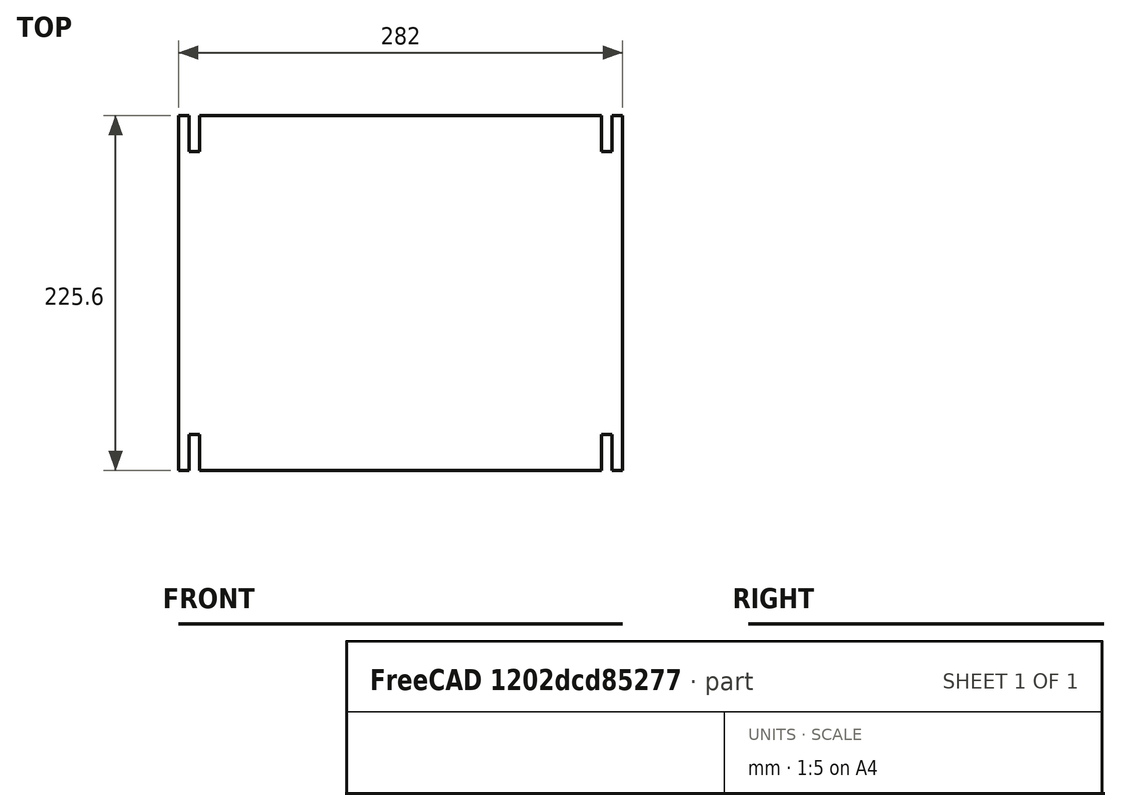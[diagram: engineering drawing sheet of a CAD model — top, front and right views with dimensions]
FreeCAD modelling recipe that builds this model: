
FCSTD DOCUMENT  (FreeCAD 0.17R13522 (Git))
Label: chamber_parts
License: All rights reserved
LicenseURL: http://en.wikipedia.org/wiki/All_rights_reserved
objects: Part::Part2DObjectPython×15, Part::FeaturePython×9, App::DocumentObjectGroup×6, Sketcher::SketchObject×3, Part::Compound×2, Part::Feature×2, Spreadsheet::Sheet×1, Part::MultiFuse×1, Drawing::FeatureViewPython×1, Drawing::FeaturePage×1, App::Part×1, Part::Cut×1
note: 33 computed .brp shape members not serialized (recipe doc carries the construction recipe); baked Part::Feature solids carry a one-line shape summary decoded from their .brp

FEATURE [Spreadsheet::Sheet] Spreadsheet  label="params"
  cells = A1=Name / alias; B1=Value; C1=Note; A2=extrusion_width; B2(extrusion_width)==20mm; A3=extrusion_x_spacer_length; B3(extrusion_spacer_length)==242mm; A4=mfc_mounting_hole_dx; B4(mfc_mounting_hole_dx)==52.710000000000001mm; C4=From MFC technical drawing (56.52 - 3.81mm); A5=mfc_mounting_hole_dy; B5(mfc_mounting_hole_dy)==20.32mm; A6=mfc_z_extent; B6(mfc_z_extent)==103.3mm; A7=mfc_y_extent; B7(mfc_y_extent)==26.68mm; A8=humidifier_bottle_diameter; B8(humidifier_bottle_diameter)==70mm; A9=humidifier_bottle_and_tube_height; B9(humidifier_bottle_and_tube_height)==230mm; A10=shelf_y_extent; B10(shelf_y_extent)==80mm; C10=Seems to need to be at least ~80mm, if I want at least 3 mounting holes, spaced with current rules.; A11=mfc_mounting_screw_clearance_diam; B11(mfc_mounting_screw_clearance_diam)==0.16950000000000001in; C11="Close fit" for 8-32; A12=mfc_x_extent; B12(mfc_x_extent)==94.950000000000003mm; A13=x_between_mfc_for_tubing; B13(x_between_mfc_for_tubing)==70mm; C13=Should allow space for 1 inlet fitting + 1 outlet fitting + the tubing to bend and get out of the way.; A14=y_mfc_to_edge_clearance; B14(y_mfc_to_edge_clearance)==14mm; C14=To allow one extrusion mounting hole to fit on other side, plus some.; A15=y_mfc_mounting_hole_center_to_edge; B15(y_mfc_mounting_hole_center_to_edge)==3.1800000000000002mm; C15=From MFC technical drawing (?); A16=x_mfc_row_offset; B16(x_mfc_row_offset)==53mm; A17=extrusion_mounting_hole_diam; B17(extrusion_mounting_hole_diam)==0.25700000000000001in; C17=max(1/4-20 clearance, M5 clearance); A18=extrusion_mounting_hole_to_edge_clearance; B18(extrusion_mounting_hole_to_edge_clearance)==4.5mm; A19=n_extrusion_mounting_holes_per_side; B19(n_extrusion_mounting_holes_per_side)=2; A20=fillet_radius; B20(fillet_radius)==4mm; A21=mfc_array_x_origin; B21(mfc_array_x_origin)==-152mm; A22=mounting_hole_spacing; B22(mounting_hole_spacing)==4.5mm; C22=Minimum amount of material along the line between two mounting holes.; A23=humidifier_bottle_spacing; B23(humidifier_bottle_spacing)==0mm; C23=Similar to above.; A24=n_humidifier_bottles; B24(n_humidifier_bottles)=4; A25=inside_plate_edge_clearance; B25(inside_plate_edge_clearance)==1.5mm; A26=extrusion_y_spacer_length; B26(extrusion_y_spacer_length)==228.59999999999999mm; A27=mounting_slot_length; B27(mounting_slot_length)==23mm; A28=shelf_x_beyond_extrusion; B28(shelf_x_beyond_extrusion)==20mm; C28=On either side (this is added to shelf x extent twice).; A29=box_height; B29(box_height)==381mm; C29=15 inches; A30=olfactometer_tube_passthru_diam; B30(olfactometer_tube_passthru_diam)==12mm; A31=chamber_support_rail_top_height; B31(chamber_support_rail_top_height)==146mm; C31=Up the length of the box_height length vertical rails.; A32=olfactometer_tube_passthru_height; B32(olfactometer_tube_passthru_height)==40mm; C32=Top of chamber support rail to center of hole.; A33=vacuum_tube_passthru_height; B33(vacuum_tube_passthru_height)==200mm; C33=Same as above.; A34=vacuum_tube_passthru_diam; B34(vacuum_tube_passthru_diam)==12mm; A35=n_mounting_holes_half_side; B35(n_mounting_holes_half_side)=5; C35=The number of mounting holes on each side of each side panel (i.e. the number in one row,  mounting to one rail).; A36=side_mounting_hole_edge_clearance; B36(side_mounting_hole_edge_clearance)==15mm
FEATURE [Part::Part2DObjectPython] Circle  label="mfc_back_mounting_hole"  # Draft 2D object (typed FeaturePython)
  FirstAngle = 0
  LastAngle = 0
  MakeFace = false
  Placement = pos=(0,20.32,0) rot=(0,0,1;0rad)
  Radius = 2.15265
  expr: Placement.Base.y = params.mfc_mounting_hole_dy
  expr: Placement.Base.x = 0
  expr: Radius = params.mfc_mounting_screw_clearance_diam / 2
FEATURE [Part::Part2DObjectPython] Circle001  label="mfc_front_mounting_hole"  # Draft 2D object (typed FeaturePython)
  FirstAngle = 0
  LastAngle = 0
  MakeFace = false
  Placement = pos=(52.71,0,0) rot=(0,0,1;0rad)
  Radius = 2.15265
  expr: Placement.Base.y = mfc_back_mounting_hole.Placement.Base.y - params.mfc_mounting_hole_dy
  expr: Placement.Base.x = mfc_back_mounting_hole.Placement.Base.x + params.mfc_mounting_hole_dx
  expr: Radius = params001.mfc_mounting_screw_clearance_diam / 2
FEATURE [Part::MultiFuse] Fusion  label="mfc_mounting_holes"
  Shapes = -> [Circle,Circle001]
  expr: Placement.Base.y = 0
  expr: Placement.Base.x = 0
FEATURE [Part::FeaturePython] Array  label="back_two_mfc_mounting_holes"  # Draft array (typed FeaturePython)
  Angle = 360
  ArrayType = 0
  Axis = (0,0,1)
  Base = -> Fusion
  Center = (0,0,0)
  Fuse = false
  IntervalAxis = (0,0,0)
  IntervalX = (164.95,0,0)
  IntervalY = (0,1,0)
  IntervalZ = (0,0,0)
  NumberPolar = 1
  NumberX = 2
  NumberY = 1
  NumberZ = 1
  Placement = pos=(-152,17.18,0) rot=(0,0,1;0rad)
  expr: Placement.Base.y = params.y_mfc_mounting_hole_center_to_edge + params.y_mfc_to_edge_clearance
  expr: Placement.Base.x = params.mfc_array_x_origin
  expr: Center.x = 0
  expr: IntervalX.x = params.mfc_x_extent + params.x_between_mfc_for_tubing
FEATURE [Part::FeaturePython] Array001  label="front_two_mfc_mounting_holes"  # Draft array (typed FeaturePython)
  Angle = 360
  ArrayType = 0
  Axis = (0,0,1)
  Base = -> Fusion
  Center = (0,0,0)
  Fuse = false
  IntervalAxis = (0,0,0)
  IntervalX = (164.95,0,0)
  IntervalY = (0,1,0)
  IntervalZ = (0,0,0)
  NumberPolar = 1
  NumberX = 2
  NumberY = 1
  NumberZ = 1
  Placement = pos=(-99,43.86,0) rot=(0,0,1;0rad)
  expr: Placement.Base.x = back_two_mfc_mounting_holes.Placement.Base.x + params.x_mfc_row_offset
  expr: Placement.Base.y = back_two_mfc_mounting_holes.Placement.Base.y + params.mfc_y_extent
  expr: Center.x = 0
  expr: IntervalX.x = params.mfc_x_extent + params.x_between_mfc_for_tubing
FEATURE [Part::Part2DObjectPython] Circle002  label="extrusion_mounting_hole"  # Draft 2D object (typed FeaturePython)
  FirstAngle = 0
  LastAngle = 0
  MakeFace = false
  Radius = 3.2639
  expr: Radius = params.extrusion_mounting_hole_diam / 2
FEATURE [Part::FeaturePython] Array002  label="extrusion_mounting_holes_left"  # Draft array (typed FeaturePython)
  Angle = 360
  ArrayType = 0
  Axis = (0,0,1)
  Base = -> Circle002
  Center = (0,0,0)
  Fuse = false
  IntervalAxis = (0,0,0)
  IntervalX = (131,0,0)
  IntervalY = (0,64.4722,0)
  IntervalZ = (0,0,0)
  NumberPolar = 1
  NumberX = 2
  NumberY = 2
  NumberZ = 1
  Placement = pos=(-131,7.7639,0) rot=(-0.894427,0,0.447214;0rad)
  expr: Placement.Base.x = -1 * (params.extrusion_spacer_length + params.extrusion_width) / 2
  expr: IntervalX.x = (params.extrusion_spacer_length + params.extrusion_width) / 2
  expr: NumberY = params.n_extrusion_mounting_holes_per_side
  expr: Placement.Base.y = params.extrusion_mounting_hole_diam / 2 + params.extrusion_mounting_hole_to_edge_clearance
  expr: IntervalY.y = (params.shelf_y_extent - params.extrusion_mounting_hole_diam - 2 * params.extrusion_mounting_hole_to_edge_clearance) / (extrusion_mounting_holes_left.NumberY - 1)
FEATURE [Part::FeaturePython] Array003  label="extrusion_mounting_holes_right"  # Draft array (typed FeaturePython)
  Angle = 360
  ArrayType = 0
  Axis = (0,0,1)
  Base = -> Circle002
  Center = (0,0,0)
  Fuse = false
  IntervalAxis = (0,0,0)
  IntervalX = (0,0,0)
  IntervalY = (0,64.4722,0)
  IntervalZ = (0,0,0)
  NumberPolar = 1
  NumberX = 1
  NumberY = 2
  NumberZ = 1
  Placement = pos=(131,7.7639,0) rot=(0,0,1;0rad)
  expr: IntervalX.x = 0
  expr: Placement.Base.y = params.extrusion_mounting_hole_diam / 2 + params.extrusion_mounting_hole_to_edge_clearance
  expr: Placement.Base.x = (params.extrusion_spacer_length + params.extrusion_width) / 2
  expr: IntervalY.y = (params.shelf_y_extent - params.extrusion_mounting_hole_diam - 2 * params.extrusion_mounting_hole_to_edge_clearance) / (extrusion_mounting_holes_right.NumberY - 1)
  expr: NumberY = 2
FEATURE [Sketcher::SketchObject] Sketch  label="mfc_shelf_outline"
  expr: Constraints[27] = params.fillet_radius
  expr: Constraints[26] = params.fillet_radius
  expr: Constraints[25] = params.fillet_radius
  expr: Constraints[12] = -1 / 2 * (params.extrusion_spacer_length + 2 * params.extrusion_width + 2 * params.shelf_x_beyond_extrusion)
  expr: Constraints[24] = params.fillet_radius
  expr: Constraints[10] = params.shelf_y_extent
  expr: Constraints[11] = params.extrusion_spacer_length + 2 * params.extrusion_width + 2 * params.shelf_x_beyond_extrusion
  sketch-geometry (10):
    g0: LineSegment StartX=-157 StartY=1e-12 StartZ=0 EndX=157 EndY=0 EndZ=0
    g1: LineSegment StartX=161 StartY=4 StartZ=0 EndX=161 EndY=76 EndZ=0
    g2: LineSegment StartX=157 StartY=80 StartZ=0 EndX=-157 EndY=80 EndZ=0
    g3: LineSegment StartX=-161 StartY=76 StartZ=0 EndX=-161 EndY=4 EndZ=0
    g4: LineSegment [constr] StartX=-123.644 StartY=80 StartZ=0 EndX=-123.644 EndY=0 EndZ=0
    g5: LineSegment [constr] StartX=-161 StartY=42.4606 StartZ=0 EndX=161 EndY=42.4606 EndZ=0
    g6: ArcOfCircle CenterX=157 CenterY=76 CenterZ=0 NormalX=0 NormalY=0 NormalZ=1 AngleXU=0 Radius=4 StartAngle=0 EndAngle=1.5708
    g7: ArcOfCircle CenterX=157 CenterY=4 CenterZ=0 NormalX=0 NormalY=0 NormalZ=1 AngleXU=0 Radius=4 StartAngle=4.71239 EndAngle=6.28319
    g8: ArcOfCircle CenterX=-157 CenterY=76 CenterZ=0 NormalX=0 NormalY=0 NormalZ=1 AngleXU=0 Radius=4 StartAngle=1.5708 EndAngle=3.14159
    g9: ArcOfCircle CenterX=-157 CenterY=4 CenterZ=0 NormalX=0 NormalY=0 NormalZ=1 AngleXU=0 Radius=4 StartAngle=3.14159 EndAngle=4.71239
  constraints (28):
    c: Vertical(g4)
    c: PointOnObject(g4,g2)
    c: PointOnObject(g4,g0)
    c: Horizontal(g5)
    c: PointOnObject(g5,g1)
    c: PointOnObject(g5,g3)
    c: Perpendicular(g2,g4)
    c: Perpendicular(g0,g4)
    c: Perpendicular(g5,g3)
    c: Perpendicular(g5,g1)
    c: Distance(g4) = 80
    c: Distance(g5) = 322
    c: DistanceX(g5) = -161
    c: DistanceY(g5) = 42.4606
    c: DistanceX(g4) = -123.644
    c: DistanceY(g4) = 0
    c: Tangent(g1,g6) = -1.5708
    c: Tangent(g2,g6) = -1.5708
    c: Tangent(g0,g7) = -1.5708
    c: Tangent(g1,g7) = -1.5708
    c: Tangent(g2,g8) = -1.5708
    c: Tangent(g3,g8) = -1.5708
    c: Tangent(g0,g9) = -1.5708
    c: Tangent(g3,g9) = -1.5708
    c: Radius(g8) = 4
    c: Radius(g6) = 4
    c: Radius(g7) = 4
    c: Radius(g9) = 4
FEATURE [Part::Part2DObjectPython] Circle003  label="hole1"  # Draft 2D object (typed FeaturePython)
  FirstAngle = 0
  LastAngle = 0
  MakeFace = false
  Placement = pos=(-11.0278,72.2361,0) rot=(0,0,1;0rad)
  Radius = 3.2639
  expr: Placement.Base.x = -1 * (params.extrusion_mounting_hole_diam + params.mounting_hole_spacing)
  expr: Placement.Base.y = extrusion_mounting_holes_left.Placement.Base.y + (params.shelf_y_extent - params.extrusion_mounting_hole_diam - 2 * params.extrusion_mounting_hole_to_edge_clearance) / (extrusion_mounting_holes_left.NumberY - 1)
  expr: Radius = params.extrusion_mounting_hole_diam / 2
FEATURE [Part::Part2DObjectPython] Circle004  label="hole2"  # Draft 2D object (typed FeaturePython)
  FirstAngle = 0
  LastAngle = 0
  MakeFace = false
  Placement = pos=(-119.972,7.7639,0) rot=(0,0,1;0rad)
  Radius = 3.2639
  expr: Placement.Base.x = -1 * (params.extrusion_spacer_length + params.extrusion_width) / 2 + params.extrusion_mounting_hole_diam + params.mounting_hole_spacing
  expr: Placement.Base.y = extrusion_mounting_holes_left.Placement.Base.y
  expr: Radius = params.extrusion_mounting_hole_diam / 2
FEATURE [Part::Part2DObjectPython] Circle005  label="hole3"  # Draft 2D object (typed FeaturePython)
  FirstAngle = 0
  LastAngle = 0
  MakeFace = false
  Placement = pos=(119.972,7.7639,0) rot=(0,0,1;0rad)
  Radius = 3.2639
  expr: Placement.Base.x = (params.extrusion_spacer_length + params.extrusion_width) / 2 - (params.extrusion_mounting_hole_diam + params.mounting_hole_spacing)
  expr: Placement.Base.y = extrusion_mounting_holes_left.Placement.Base.y
  expr: Radius = params.extrusion_mounting_hole_diam / 2
FEATURE [Part::Part2DObjectPython] Circle006  label="hole4"  # Draft 2D object (typed FeaturePython)
  FirstAngle = 0
  LastAngle = 0
  MakeFace = false
  Placement = pos=(119.972,72.2361,0) rot=(0,0,1;0rad)
  Radius = 3.2639
  expr: Placement.Base.x = (params.extrusion_spacer_length + params.extrusion_width) / 2 - (params.extrusion_mounting_hole_diam + params.mounting_hole_spacing)
  expr: Placement.Base.y = extrusion_mounting_holes_left.Placement.Base.y + (params.shelf_y_extent - params.extrusion_mounting_hole_diam - 2 * params.extrusion_mounting_hole_to_edge_clearance) / (extrusion_mounting_holes_left.NumberY - 1)
  expr: Radius = params.extrusion_mounting_hole_diam / 2
FEATURE [Sketcher::SketchObject] Sketch001  label="humidifier_shelf_outline"
  expr: Constraints[27] = params.fillet_radius
  expr: Constraints[26] = params.fillet_radius
  expr: Constraints[25] = params.fillet_radius
  expr: Constraints[24] = params.fillet_radius
  expr: Constraints[10] = params.shelf_y_extent
  expr: Constraints[11] = params.extrusion_spacer_length + 2 * params.extrusion_width
  sketch-geometry (10):
    g0: LineSegment StartX=-137 StartY=0 StartZ=0 EndX=137 EndY=0 EndZ=0
    g1: LineSegment StartX=141 StartY=4 StartZ=0 EndX=141 EndY=76 EndZ=0
    g2: LineSegment StartX=137 StartY=80 StartZ=0 EndX=-137 EndY=80 EndZ=0
    g3: LineSegment StartX=-141 StartY=76 StartZ=0 EndX=-141 EndY=4 EndZ=0
    g4: LineSegment [constr] StartX=-123.644 StartY=80 StartZ=0 EndX=-123.644 EndY=0 EndZ=0
    g5: LineSegment [constr] StartX=-141 StartY=42.4606 StartZ=0 EndX=141 EndY=42.4606 EndZ=0
    g6: ArcOfCircle CenterX=137 CenterY=76 CenterZ=0 NormalX=0 NormalY=0 NormalZ=1 AngleXU=0 Radius=4 StartAngle=0 EndAngle=1.5708
    g7: ArcOfCircle CenterX=137 CenterY=4 CenterZ=0 NormalX=0 NormalY=0 NormalZ=1 AngleXU=0 Radius=4 StartAngle=4.71239 EndAngle=6.28319
    g8: ArcOfCircle CenterX=-137 CenterY=76 CenterZ=0 NormalX=0 NormalY=0 NormalZ=1 AngleXU=0 Radius=4 StartAngle=1.5708 EndAngle=3.14159
    g9: ArcOfCircle CenterX=-137 CenterY=4 CenterZ=0 NormalX=0 NormalY=0 NormalZ=1 AngleXU=0 Radius=4 StartAngle=3.14159 EndAngle=4.71239
  constraints (28):
    c: Vertical(g4)
    c: PointOnObject(g4,g2)
    c: PointOnObject(g4,g0)
    c: Horizontal(g5)
    c: PointOnObject(g5,g1)
    c: PointOnObject(g5,g3)
    c: Perpendicular(g2,g4)
    c: Perpendicular(g0,g4)
    c: Perpendicular(g5,g3)
    c: Perpendicular(g5,g1)
    c: Distance(g4) = 80
    c: Distance(g5) = 282
    c: DistanceX(g5) = -141
    c: DistanceY(g5) = 42.4606
    c: DistanceX(g4) = -123.644
    c: DistanceY(g4) = 0
    c: Tangent(g1,g6) = -1.5708
    c: Tangent(g2,g6) = -1.5708
    c: Tangent(g0,g7) = -1.5708
    c: Tangent(g1,g7) = -1.5708
    c: Tangent(g2,g8) = -1.5708
    c: Tangent(g3,g8) = -1.5708
    c: Tangent(g0,g9) = -1.5708
    c: Tangent(g3,g9) = -1.5708
    c: Radius(g8) = 4
    c: Radius(g6) = 4
    c: Radius(g7) = 4
    c: Radius(g9) = 4
FEATURE [Part::Compound] Compound001  label="extrusion_mounting_holes_compound"
  Links = -> [Array003,Array002]
FEATURE [Part::Compound] Compound002  label="extra_mounting_holes_compound"
  Links = -> [Circle003,Circle004,Circle005,Circle006]
FEATURE [App::DocumentObjectGroup] Group002  label="mfc_mounting_plate"
  Group = -> [Sketch,Compound001,Compound002,Array,Array001]
FEATURE [Drawing::FeatureViewPython] ViewGroup002  # drawing view (typed FeaturePython)
  AlwaysOn = false
  Direction = (0,0,0)
  FillStyle = 0
  FontSize = 12
  LineSpacing = 0
  LineStyle = 0
  LineWidth = 0.35
  Rotation = 0
  Source = -> Group002
  ViewResult = <g id="ViewGroup002" transform="rotate(0.0,150.0,150.0) translate(150.0,150.0) scale(1.0,-1.0)"></g>
  Visible = false
  X = 150
  Y = 150
FEATURE [Drawing::FeaturePage] Page  label="printable_view"
  EditableTexts = DRAW_BY | CONTROLLED_BY | DATE | Controlled 2: | CONTROLLED 2 | Controlled 3: | CONTROLLED 3 | SCALE | MOD | COMPANY | ADRESS | COUNTRY | PART NAME | PROJECT NUMBER | A: | A_ | B: | B_ | C: | C_ | D: | D_ | E: | E_ | Quantity | Part ID / number | Fabrication tolerances | Material | 01 | 001 - 001 | ISO2768 - fH | IRON
  Group = -> [ViewGroup002]
  Template = <path>
FEATURE [Sketcher::SketchObject] Sketch002  label="humidifier_bottle_guide_outline"
  expr: Constraints[27] = params.fillet_radius
  expr: Constraints[26] = params.fillet_radius
  expr: Constraints[25] = params.fillet_radius
  expr: Constraints[24] = params.fillet_radius
  expr: Constraints[10] = params.shelf_y_extent
  expr: Constraints[11] = params.extrusion_spacer_length + 2 * params.extrusion_width
  sketch-geometry (10):
    g0: LineSegment StartX=-137 StartY=0 StartZ=0 EndX=137 EndY=0 EndZ=0
    g1: LineSegment StartX=141 StartY=4 StartZ=0 EndX=141 EndY=76 EndZ=0
    g2: LineSegment StartX=137 StartY=80 StartZ=0 EndX=-137 EndY=80 EndZ=0
    g3: LineSegment StartX=-141 StartY=76 StartZ=0 EndX=-141 EndY=4 EndZ=0
    g4: LineSegment [constr] StartX=-123.644 StartY=80 StartZ=0 EndX=-123.644 EndY=0 EndZ=0
    g5: LineSegment [constr] StartX=-141 StartY=42.4606 StartZ=0 EndX=141 EndY=42.4606 EndZ=0
    g6: ArcOfCircle CenterX=137 CenterY=76 CenterZ=0 NormalX=0 NormalY=0 NormalZ=1 AngleXU=0 Radius=4 StartAngle=0 EndAngle=1.5708
    g7: ArcOfCircle CenterX=137 CenterY=4 CenterZ=0 NormalX=0 NormalY=0 NormalZ=1 AngleXU=0 Radius=4 StartAngle=4.71239 EndAngle=6.28319
    g8: ArcOfCircle CenterX=-137 CenterY=76 CenterZ=0 NormalX=0 NormalY=0 NormalZ=1 AngleXU=0 Radius=4 StartAngle=1.5708 EndAngle=3.14159
    g9: ArcOfCircle CenterX=-137 CenterY=4 CenterZ=0 NormalX=0 NormalY=0 NormalZ=1 AngleXU=0 Radius=4 StartAngle=3.14159 EndAngle=4.71239
  constraints (28):
    c: Vertical(g4)
    c: PointOnObject(g4,g2)
    c: PointOnObject(g4,g0)
    c: Horizontal(g5)
    c: PointOnObject(g5,g1)
    c: PointOnObject(g5,g3)
    c: Perpendicular(g2,g4)
    c: Perpendicular(g0,g4)
    c: Perpendicular(g5,g3)
    c: Perpendicular(g5,g1)
    c: Distance(g4) = 80
    c: Distance(g5) = 282
    c: DistanceX(g5) = -141
    c: DistanceY(g5) = 42.4606
    c: DistanceX(g4) = -123.644
    c: DistanceY(g4) = 0
    c: Tangent(g1,g6) = -1.5708
    c: Tangent(g2,g6) = -1.5708
    c: Tangent(g0,g7) = -1.5708
    c: Tangent(g1,g7) = -1.5708
    c: Tangent(g2,g8) = -1.5708
    c: Tangent(g3,g8) = -1.5708
    c: Tangent(g0,g9) = -1.5708
    c: Tangent(g3,g9) = -1.5708
    c: Radius(g8) = 4
    c: Radius(g6) = 4
    c: Radius(g7) = 4
    c: Radius(g9) = 4
FEATURE [Part::Part2DObjectPython] Circle007  label="bottle_space"  # Draft 2D object (typed FeaturePython)
  FirstAngle = 0
  LastAngle = 0
  MakeFace = false
  Placement = pos=(35,0,0) rot=(0,0,1;0rad)
  Radius = 35
  expr: Placement.Base.x = params.humidifier_bottle_diameter / 2
  expr: Radius = params.humidifier_bottle_diameter / 2
FEATURE [Part::FeaturePython] Array004  label="bottles_space1"  # Draft array (typed FeaturePython)
  Angle = 360
  ArrayType = 0
  Axis = (0,0,1)
  Base = -> Circle007
  Center = (0,0,0)
  Fuse = false
  IntervalAxis = (0,0,0)
  IntervalX = (70,0,0)
  IntervalY = (0,1,0)
  IntervalZ = (0,0,0)
  NumberPolar = 1
  NumberX = 4
  NumberY = 1
  NumberZ = 1
  Placement = pos=(-140,40,0) rot=(0,0,1;0rad)
  expr: Placement.Base.x = -1 / 2 * (params.n_humidifier_bottles * params.humidifier_bottle_diameter + (params.n_humidifier_bottles - 1) * params.humidifier_bottle_spacing)
  expr: Placement.Base.y = params.shelf_y_extent / 2
  expr: IntervalX.x = params.humidifier_bottle_diameter + params.humidifier_bottle_spacing
FEATURE [Part::FeaturePython] Clone  label="humidifier_extrusion_mounting_holes"  # Draft clone (typed FeaturePython)
  AttacherType = Attacher::AttachEngine3D
  Fuse = false
  Objects = -> [Compound001]
  Scale = (1,1,1)
FEATURE [Part::Part2DObjectPython] Circle008  label="humidifier_hole1"  # Draft 2D object (typed FeaturePython)
  FirstAngle = 0
  LastAngle = 0
  MakeFace = false
  Radius = 3.2639
  expr: Placement.Base.x = 0
  expr: Placement.Base.y = 0
  expr: Radius = params.extrusion_mounting_hole_diam / 2
FEATURE [Part::FeaturePython] Array005  label="humifier_extra_mounting_holes"  # Draft array (typed FeaturePython)
  Angle = 360
  ArrayType = 0
  Axis = (0,0,1)
  Base = -> Circle008
  Center = (0,0,0)
  Fuse = false
  IntervalAxis = (0,0,0)
  IntervalX = (140,0,0)
  IntervalY = (0,64.4722,0)
  IntervalZ = (0,0,0)
  NumberPolar = 1
  NumberX = 2
  NumberY = 2
  NumberZ = 1
  Placement = pos=(-70,7.7639,0) rot=(0,0,1;0rad)
  expr: IntervalY.y = params.shelf_y_extent - 2 * params.extrusion_mounting_hole_to_edge_clearance - params.extrusion_mounting_hole_diam
  expr: Placement.Base.y = params.extrusion_mounting_hole_to_edge_clearance + params.extrusion_mounting_hole_diam / 2
  expr: Placement.Base.x = -1 * (params.humidifier_bottle_diameter + params.humidifier_bottle_spacing / 2)
  expr: IntervalX.x = 2 * params.humidifier_bottle_diameter + params.humidifier_bottle_spacing
FEATURE [App::DocumentObjectGroup] Group  label="humidifier_mounting_holes"
  Group = -> [Clone,Circle008,Array005]
FEATURE [App::DocumentObjectGroup] Group004  label="humidifier_bottles_mount"
  Group = -> [Sketch001,Sketch002,Circle007,Array004,Group]
FEATURE [Part::Part2DObjectPython] Rectangle001  label="mounting_slot"  # Draft 2D object (typed FeaturePython)
  ChamferSize = 0
  Columns = 1
  FilletRadius = 0
  Height = 23
  Length = 6.5278
  MakeFace = false
  Rows = 1
  expr: Height = params.mounting_slot_length
  expr: Length = params.extrusion_mounting_hole_diam
FEATURE [Part::FeaturePython] Array006  label="inside_plate_mounting_slots"  # Draft array (typed FeaturePython)
  Angle = 360
  ArrayType = 0
  Axis = (0,0,1)
  Base = -> Rectangle001
  Center = (0,0,0)
  Fuse = false
  IntervalAxis = (0,0,0)
  IntervalX = (262,0,0)
  IntervalY = (0,202.6,0)
  IntervalZ = (0,0,0)
  NumberPolar = 1
  NumberX = 2
  NumberY = 2
  NumberZ = 1
  Placement = pos=(6.7361,0,0) rot=(0,0,1;0rad)
  expr: IntervalX.x = params.extrusion_width + params.extrusion_spacer_length
  expr: IntervalY.y = params.extrusion_y_spacer_length - params.mounting_slot_length - params.inside_plate_edge_clearance * 2
  expr: Placement.Base.x = (params.extrusion_width - params.extrusion_mounting_hole_diam) / 2
FEATURE [Part::Part2DObjectPython] Rectangle  label="diffuser_outline"  # Draft 2D object (typed FeaturePython)
  ChamferSize = 0
  Columns = 1
  FilletRadius = 0
  Height = 225.6
  Length = 282
  MakeFace = false
  Rows = 1
  expr: Length = params.extrusion_spacer_length + 2 * params.extrusion_width
  expr: Height = params.extrusion_y_spacer_length - 2 * params.inside_plate_edge_clearance
FEATURE [App::Part] Part  label="diffuser_plate"
  Group = -> [Rectangle,Rectangle001,Array006]
  License = CC BY 3.0
  LicenseURL = http://creativecommons.org/licenses/by/3.0/
  Origin = -> Origin
FEATURE [Part::Feature] Face  label="inside_plate"
  shape: bbox 282 x 225.6 x 2e-07 mm, 1 faces, 0 solids (baked)
FEATURE [Part::Feature] Shell  label="mounting_slots"
  shape: bbox 268.5 x 225.6 x 2e-07 mm, 4 faces, 0 solids (baked)
FEATURE [Part::Cut] Cut  label="inside_plate_with_slots"
  Base = -> Face
  Tool = -> Shell
FEATURE [App::DocumentObjectGroup] Group005  label="diffuser_plate01"
  Group = -> [Part,Cut]
FEATURE [App::DocumentObjectGroup] Group007  label="box_back"
FEATURE [Part::Part2DObjectPython] Rectangle002  label="side_outline_base"  # Draft 2D object (typed FeaturePython)
  ChamferSize = 0
  Columns = 1
  FilletRadius = 5
  Height = 381
  Length = 268.6
  MakeFace = false
  Placement = pos=(-134.3,0,0) rot=(0,0,1;0rad)
  Rows = 1
  expr: Placement.Base.y = 0
  expr: Length = params.extrusion_y_spacer_length + 2 * params.extrusion_width
  expr: Placement.Base.x = -1 / 2 * side_outline_base.Length
  expr: Height = params.box_height
FEATURE [Part::Part2DObjectPython] Circle009  label="olfactometer_tube_passthru"  # Draft 2D object (typed FeaturePython)
  FirstAngle = 0
  LastAngle = 0
  MakeFace = false
  Placement = pos=(0,192,0) rot=(0,0,1;0rad)
  Radius = 6
  expr: Placement.Base.y = params.olfactometer_tube_passthru_diam / 2 + params.chamber_support_rail_top_height + params.olfactometer_tube_passthru_height
  expr: Radius = params.olfactometer_tube_passthru_diam / 2
FEATURE [Part::Part2DObjectPython] Circle010  label="vacuum_tube_passthru"  # Draft 2D object (typed FeaturePython)
  FirstAngle = 0
  LastAngle = 0
  MakeFace = false
  Placement = pos=(0,352,0) rot=(0,0,1;0rad)
  Radius = 6
  expr: Placement.Base.y = params.vacuum_tube_passthru_diam / 2 + params.chamber_support_rail_top_height + params.vacuum_tube_passthru_height
  expr: Radius = params.vacuum_tube_passthru_diam / 2
FEATURE [Part::Part2DObjectPython] Circle011  label="side_extrusion_mounting_hole"  # Draft 2D object (typed FeaturePython)
  FirstAngle = 0
  LastAngle = 0
  MakeFace = false
  Radius = 3.2639
  expr: Radius = params.extrusion_mounting_hole_diam / 2
FEATURE [Part::FeaturePython] Array007  label="side_extrusion_mounting_holes"  # Draft array (typed FeaturePython)
  Angle = 360
  ArrayType = 0
  Axis = (0,0,1)
  Base = -> Circle011
  Center = (0,0,0)
  Fuse = false
  IntervalAxis = (0,0,0)
  IntervalX = (248.6,0,0)
  IntervalY = (0,86.118,0)
  IntervalZ = (0,0,0)
  NumberPolar = 1
  NumberX = 2
  NumberY = 5
  NumberZ = 1
  Placement = pos=(-124.3,18.2639,0) rot=(0,0,1;0rad)
  expr: Placement.Base.y = params.side_mounting_hole_edge_clearance + params.extrusion_mounting_hole_diam / 2
  expr: IntervalX.x = params.extrusion_y_spacer_length + params.extrusion_width
  expr: NumberY = params.n_mounting_holes_half_side
  expr: IntervalY.y = (params.box_height - params.extrusion_mounting_hole_diam - 2 * params.side_mounting_hole_edge_clearance) / (params.n_mounting_holes_half_side - 1)
  expr: Placement.Base.x = -1 / 2 * (params.extrusion_y_spacer_length + params.extrusion_width)
FEATURE [App::DocumentObjectGroup] Group006  label="box_sides"
  Group = -> [Rectangle002,Circle009,Circle010,Circle011,Array007]
note: 1 file-system path scrubbed to <path> (originals preserved in the JSON sidecar)
